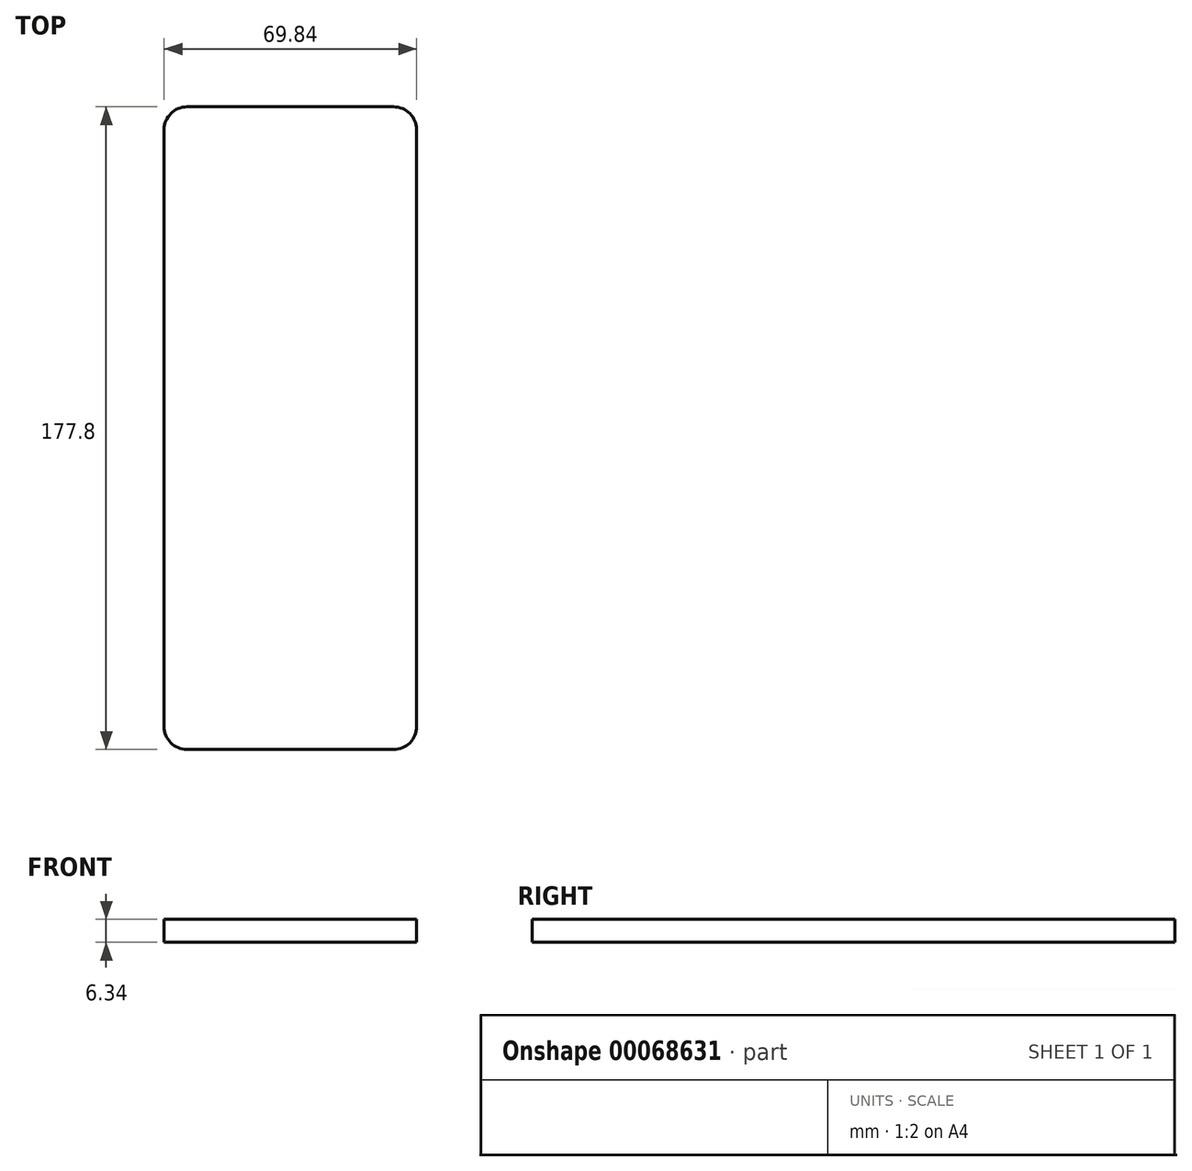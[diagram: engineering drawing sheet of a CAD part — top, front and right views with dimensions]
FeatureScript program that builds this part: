
annotation { "Feature Type Name" : "Feature", "Feature Type Description" : "" }
export const myFeature = defineFeature(function(context is Context, id is Id, definition is map)
    precondition{}
    {
        {
            var Q0;
            Q0=qCreatedBy(makeId("Top.planeOp"),FACE);
            var sketch = newSketch(context, id + "F0", { "sketchPlane" : qUnion([Q0])});
            skLineSegment(sketch, "E0.bottom", {"start": v(-28.58, 88.9) * mm, "end": v(28.58, 88.9) * mm});
            skLineSegment(sketch, "E0.top", {"start": v(-28.58, -88.9) * mm, "end": v(28.58, -88.9) * mm});
            skLineSegment(sketch, "E0.left", {"start": v(-34.93, 82.55) * mm, "end": v(-34.93, -82.55) * mm});
            skLineSegment(sketch, "E0.right", {"start": v(34.93, 82.55) * mm, "end": v(34.93, -82.55) * mm});
            skPoint(sketch, "E1.visualSharp", {"position": v(-34.93, 88.9) * mm});
            skArc(sketch, "E1.filletArc", {"start": v(-28.58, 88.9) * mm, "mid": v(-33.07, 87.04) * mm, "end": v(-34.93, 82.55) * mm});
            skPoint(sketch, "E2.visualSharp", {"position": v(-34.93, -88.9) * mm});
            skArc(sketch, "E2.filletArc", {"start": v(-34.93, -82.55) * mm, "mid": v(-33.07, -87.04) * mm, "end": v(-28.58, -88.9) * mm});
            skPoint(sketch, "E3.visualSharp", {"position": v(34.93, -88.9) * mm});
            skArc(sketch, "E3.filletArc", {"start": v(28.58, -88.9) * mm, "mid": v(33.07, -87.04) * mm, "end": v(34.93, -82.55) * mm});
            skPoint(sketch, "E4.visualSharp", {"position": v(34.93, 88.9) * mm});
            skArc(sketch, "E4.filletArc", {"start": v(34.93, 82.55) * mm, "mid": v(33.07, 87.04) * mm, "end": v(28.58, 88.9) * mm});
            skSolve(sketch);
        }
        {
            var Q0;
            Q0=makeQuery(id+"F0.imprint","IMPRINT",FACE,{"disambiguationData":[TD([[makeQuery(id+"F0.imprint","IMPRINT",EDGE,{"derivedFrom":sQuery(id+"F0.wireOp",EDGE,"E0.bottom")}),-1.0]])]});
            extrude(context, id + "F1", {"entities" : qUnion([Q0]), "endBound" : BoundingType.SYMMETRIC, "depth" : 6.35 * mm});
        }
    });
